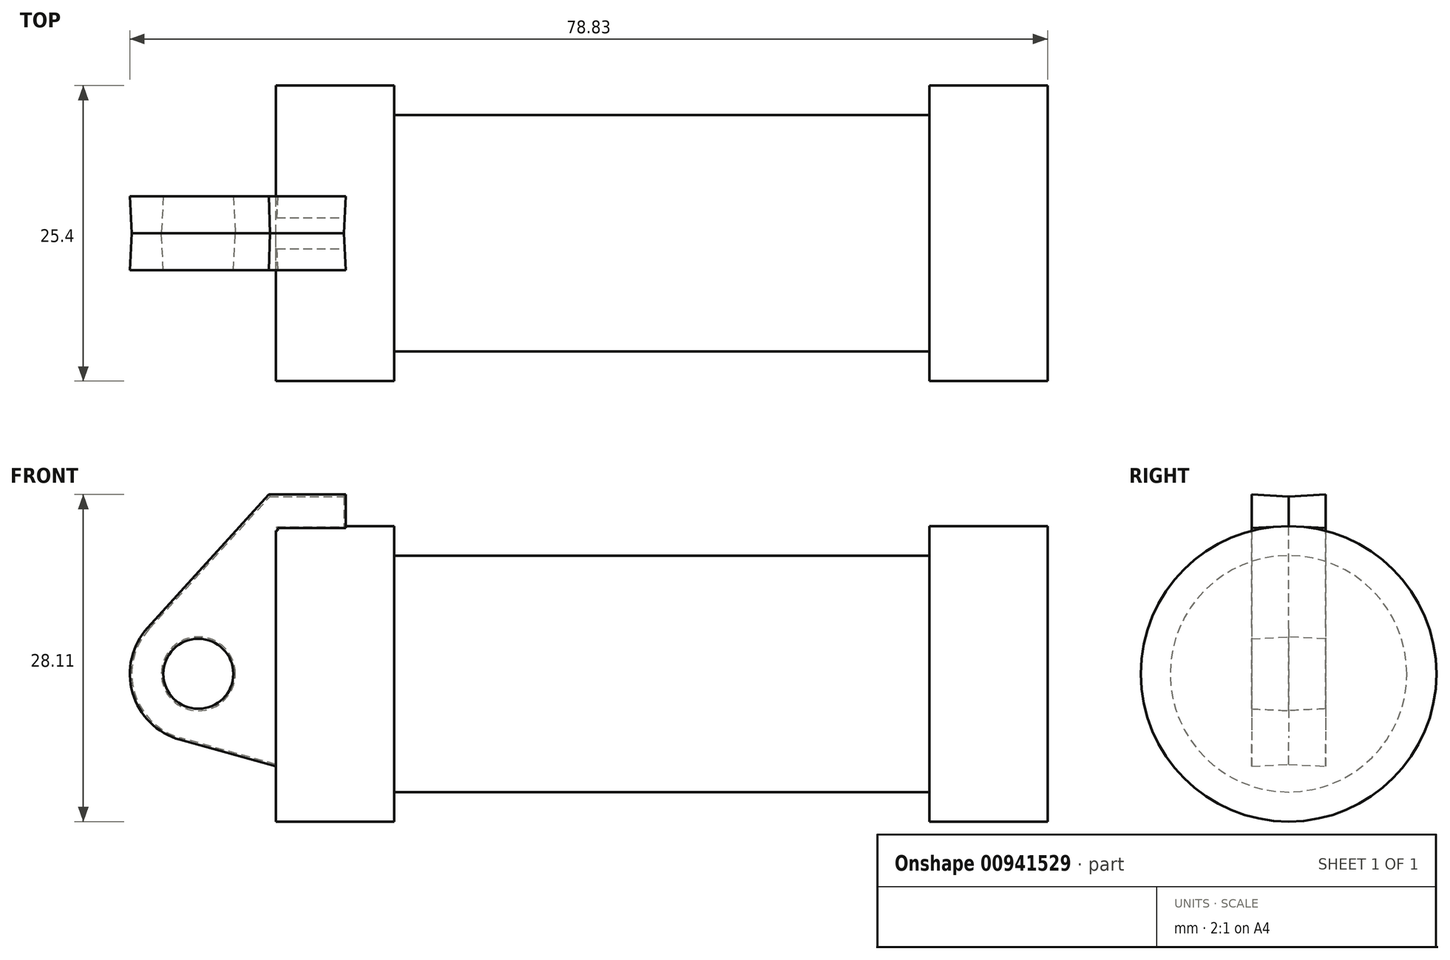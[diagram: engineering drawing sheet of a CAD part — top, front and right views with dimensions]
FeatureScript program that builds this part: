
annotation { "Feature Type Name" : "Feature", "Feature Type Description" : "" }
export const myFeature = defineFeature(function(context is Context, id is Id, definition is map)
    precondition{}
    {
        {
            var Q0;
            Q0=qCreatedBy(makeId("Front.planeOp"),FACE);
            var sketch = newSketch(context, id + "F0", { "sketchPlane" : qUnion([Q0])});
            skLineSegment(sketch, "E0", {"start": v(0, 0) * mm, "end": v(0, 12.7) * mm});
            skLineSegment(sketch, "E1", {"start": v(0, 12.7) * mm, "end": v(10.16, 12.7) * mm});
            skLineSegment(sketch, "E2", {"start": v(10.16, 12.7) * mm, "end": v(10.16, 10.16) * mm});
            skLineSegment(sketch, "E3", {"start": v(10.16, 10.16) * mm, "end": v(56.13, 10.16) * mm});
            skLineSegment(sketch, "E4", {"start": v(56.13, 10.16) * mm, "end": v(56.13, 12.7) * mm});
            skLineSegment(sketch, "E5", {"start": v(56.13, 12.7) * mm, "end": v(66.3, 12.7) * mm});
            skLineSegment(sketch, "E6", {"start": v(66.3, 12.7) * mm, "end": v(66.3, 0) * mm});
            skLineSegment(sketch, "E7", {"start": v(66.3, 0) * mm, "end": v(0, 0) * mm});
            skLineSegment(sketch, "E8", {"start": v(5.84, 15.24) * mm, "end": v(-0.5, 15.24) * mm});
            skLineSegment(sketch, "E9", {"start": v(-0.5, 15.24) * mm, "end": v(-10.88, 3.85) * mm});
            skLineSegment(sketch, "E10", {"start": v(0, 0) * mm, "end": v(-6.65, 0) * mm});
            skCircle(sketch, "E11", {"center": v(-6.65, 0) * mm, "radius": 5.72 * mm});
            skCircle(sketch, "E12", {"center": v(-6.65, 0) * mm, "radius": 3.18 * mm});
            skLineSegment(sketch, "E13", {"start": v(5.84, 15.24) * mm, "end": v(5.84, -9.4) * mm});
            skLineSegment(sketch, "E14", {"start": v(5.84, -9.4) * mm, "end": v(-8.18, -5.5) * mm});
            skSolve(sketch);
        }
        {
            var Q0;
            {var subQ0=sQuery(id+"F0.wireOp",EDGE,"E0");Q0=makeQuery(id+"F0.imprint","IMPRINT",FACE,{"disambiguationData":[TD([[makeQuery(id+"F0.imprint","IMPRINT",EDGE,{"derivedFrom":subQ0}),-1.0]])]});}
            var Q1;
            {var subQ0=sQuery(id+"F0.wireOp",EDGE,"E2");Q1=makeQuery(id+"F0.imprint","IMPRINT",FACE,{"disambiguationData":[TD([[makeQuery(id+"F0.imprint","IMPRINT",EDGE,{"derivedFrom":subQ0}),-1.0]])]});}
            var Q2;
            Q2=sQuery(id+"F0.wireOp",EDGE,"E7");
            revolve(context, id + "F1", {"surfaceOperationType" : NewSurfaceOperationType.NEW, "entities" : qUnion([Q0, Q1]), "axis" : qUnion([Q2]), "revolveType" : RevolveType.FULL});
        }
        {
            var Q0;
            Q0 = qSketchRegion(id + "FovCr3BdbOmw2TF_1", true);
            var Q1;
            {var subQ1=sQuery(id+"F0.wireOp",EDGE,"E0");Q1=makeQuery(id+"F0.imprint","IMPRINT",FACE,{"disambiguationData":[TD([[makeQuery(id+"F0.imprint","IMPRINT",EDGE,{"derivedFrom":subQ1}),1.0]])]});}
            var Q2;
            {var subQ5=sQuery(id+"F0.wireOp",EDGE,"E12");Q2=makeQuery(id+"F0.imprint","IMPRINT",FACE,{"disambiguationData":[TD([[makeQuery(id+"F0.imprint","IMPRINT",EDGE,{"derivedFrom":subQ5}),-1.0]])]});}
            var Q3;
            {var subQ0=sQuery(id+"F0.wireOp",EDGE,"E14");Q3=makeQuery(id+"F0.imprint","IMPRINT",FACE,{"disambiguationData":[TD([[makeQuery(id+"F0.imprint","IMPRINT",EDGE,{"derivedFrom":subQ0}),-1.0]])]});}
            extrude(context, id + "F2", {"entities" : qUnion([Q0, Q1, Q2, Q3]), "operationType" : NewBodyOperationType.ADD, "endBound" : BoundingType.SYMMETRIC, "depth" : 6.35 * mm, "offsetDistance" : 25.4 * mm, "hasDraft" : true, "draftAngle" : 3 * degree});
        }
    });
